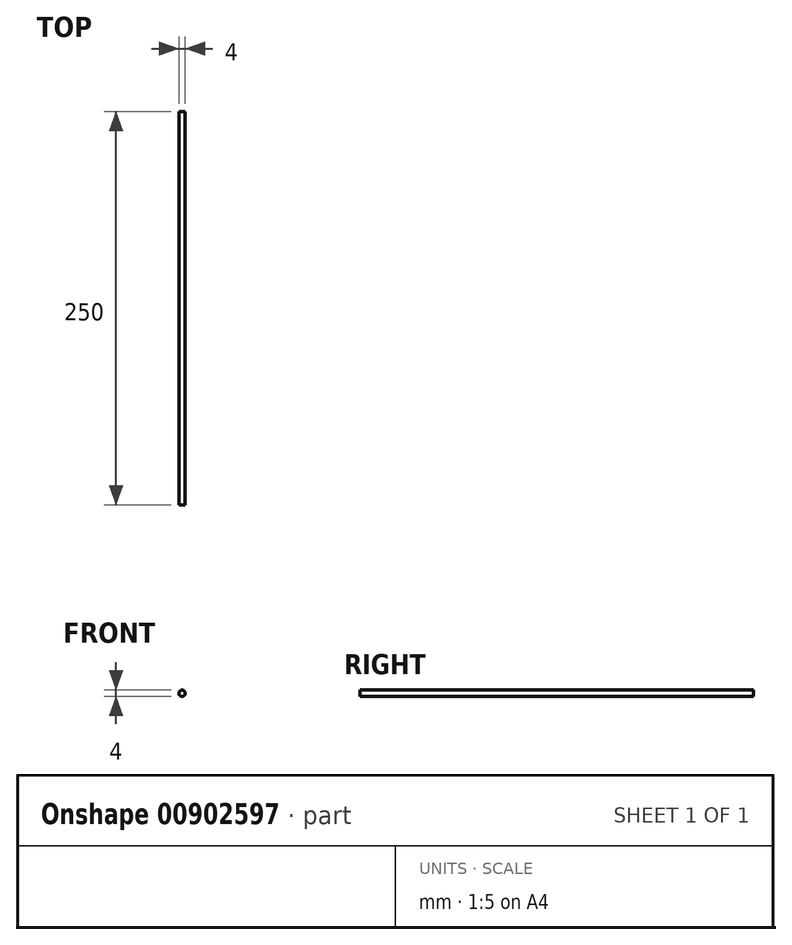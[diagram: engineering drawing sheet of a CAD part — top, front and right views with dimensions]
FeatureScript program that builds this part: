
annotation { "Feature Type Name" : "Feature", "Feature Type Description" : "" }
export const myFeature = defineFeature(function(context is Context, id is Id, definition is map)
    precondition{}
    {
        {
            var Q0;
            Q0=qCreatedBy(makeId("Front.planeOp"),FACE);
            var sketch = newSketch(context, id + "F0", { "sketchPlane" : qUnion([Q0])});
            skCircle(sketch, "E0", {"center": v(0, 0) * mm, "radius": 2 * mm});
            skSolve(sketch);
        }
        {
            var Q0;
            Q0 = qSketchRegion(id + "F0", true);
            extrude(context, id + "F1", {"entities" : qUnion([Q0]), "endBound" : BoundingType.SYMMETRIC, "depth" : 250 * mm, "offsetDistance" : 25 * mm});
        }
    });
